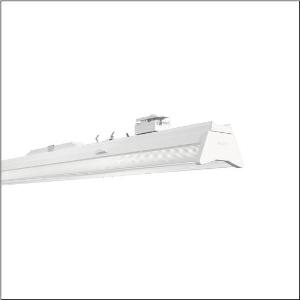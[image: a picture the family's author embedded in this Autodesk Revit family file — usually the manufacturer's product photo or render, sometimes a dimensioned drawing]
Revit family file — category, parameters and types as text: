
# Revit family: licross_r__21_performance_ho_52td16cn4c5m_c92a
name_source: partatom
category: Lighting Fixtures
units: mm (PartAtom-declared; Revit-internal decimal feet)

## family parameters
Cut with Voids When Loaded = No
Host = Face
Light Source = No
Part Type = Normal
Room Calculation Point = No
Round Connector Dimension = Use Diameter
Shared = No

## types (1)
- --- (1 x LED, 12610 lm, 68.9 W, 4000K)
    Apparent Load = 69 VA
    CIE Flux Codes = 63 87 95 78 100
    Color Rendering = 80
    Color Temperature = 4000K
    Default Elevation = 1800 mm
    Description = Licross® 21 Performance HO, luminaire insert, of sheet steel, galvanised, coil coated, white, length: 1.500mm, width: 120mm, height: 123mm, LED rated luminous flux: 12.610lm, light colour: 840, control gear: ON/OFF Multilumen, CLOi, control gear: ECG Multilumen, with plug, 3-pole, with phase selection, mains connection: 220..240V, AC, 50/60Hz, start of lifetime: 69W, end of service life: 83W, halogen-free wiring, primary light control with lens, of plastic, primary optical cover: cover, of PMMA, light emission: direct/indirect distribution, primary light characteristic: symmetric, protection rating (complete): IP54, insulation class (complete): insulation class I (protective earthing), certification: CE, ENEC, UKCA, protection symbol: D if used in an environment with non-conductive dust loads with corresponding accessories, impact resistance: IK06, permissible ambient temperature for indoor applications: -35..+35°C, corresponds to IFS (International Featured Standards) requirements for safety and quality in the food industry, reducing of maximum allowable ambient temperature of 5°C with ceiling mounting, LABS conformity tested according to VDMA 24364:2018-05, packaging unit: 1 piece
    Height = 114 mm
    Lamp = 1 x LED
    Lamp Light Flux = 12610 lm
    Lamp Power = 68.9 W
    Lamp count = 1
    Length = 1500 mm
    Luminous efficacy = 183 lm/W
    Manufacturer = Siteco
    ModVariant = No
    Model = 52TD16CN4C5M
    Mounting Place = Ceiling
    Mounting Type = Pendant
    Number of Poles = 1
    OnlyDefault = Yes
    Power Factor = 1
    Product Name = Licross® 21 Performance HO
    Product group = luminaire insert
    ProductGroupID = 901
    Protection Class = Protection class I
    Protection Degree = IP 54
    RLX_Detail_Level = 1
    RLX_Emergency_Light_Flux = 0 lm
    RLX_Emergency_Type = 0
    RLX_Emergency_Type_DB = No
    RlxData = <blob elided: 31817 chars, md5=c6dba0c7>
    Socket = socket
    Standby Power = 0 W
    System Light Flux = 12610 lm
    System Power = 69 W
    Type Comments = factory setting: luminous flux: 100 % | (A | C | E) | 162 mA
    Type Image = l_1256138.jpg
    URL = http://relux.com
    VarID = @adj_059855
    Voltage = 0 V
    Weight = 0.00 kg
    Width = 120 mm

## geometry (parser evidence)
native form markers: Blend x4, Sweep x11
no freeform markers — native parametric forms only
